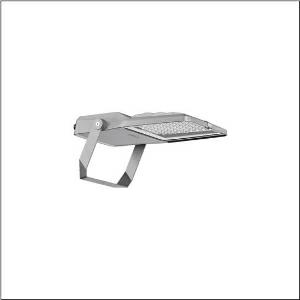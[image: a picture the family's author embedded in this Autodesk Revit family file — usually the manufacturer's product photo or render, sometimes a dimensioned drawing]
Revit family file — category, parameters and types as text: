
# Revit family: floodlight_fl_21_iq_mini___rs12_5xa7772c2b1a_7425
name_source: partatom
category: Lighting Fixtures
units: mm (PartAtom-declared; Revit-internal decimal feet)

## family parameters
Cut with Voids When Loaded = No
Host = Face
Light Source = No
Part Type = Normal
Room Calculation Point = No
Round Connector Dimension = Use Diameter
Shared = No

## types (1)
- --- (1 x LED, 12340 lm, 87.2 W, 3000K)
    Apparent Load = 87 VA
    CIE Flux Codes = 79 92 99 100 100
    Color Rendering = 70
    Color Temperature = 3000K
    Default Elevation = 1800 mm
    Description = Floodlight FL 21 iQ mini, floodlight, primary light control with lens, of PMMA, primary optical cover: protective disc, of toughened safety glass, transparent, light distribution: RS12, light emission: direct distribution, installation type: surface-mounted, LED, High Power LED, rated luminous flux: 12.340lm, luminous efficacy: 142lm/W, light colour: 730, colour temperature: 3000K, control gear: iQ Street-Remote/DALI, control: Street-Remote, Auto-Match, Temp-Guard, Night-Set, Smart-Wire, Desk-Remote (wireless, voltage-free reading and setting of iQ features in the workshop via application-optimized NFC function/RFID function), optimised constant luminous flux control (CLO 2.0), with terminal, 6-pole, mains connection: 220..240V, AC, 50/60Hz, start of lifetime: 87W, end of service life: 92W, reduction: 40W, luminaire housing, of diecast aluminium, powder-coated, Siteco® metallic grey (DB 702S), corrosivity category C5 mid according to DIN EN ISO 12944, suitable for swimming pools, chlorine-resistant, sealing non-destructively replaceable, mounting bracket, of steel, galvanised, powder-coated, Siteco® metallic grey (DB 702S), protection rating (complete): IP66, insulation class (complete): insulation class II (safety insulation), certification: CE, ENEC, VDE, protection symbol: D, impact resistance: IK08, permissible operating ambient temperature: -40..+40°C, permissible operating ambient temperature for outdoor applications: -40..+50°C, standard: DIN EN 12944, LABS conformity tested according to VDMA 24364:2018-05, packaging unit: 1 piece

Light Distribution: RS12
    Height = 70 mm
    Lamp = 1 x LED
    Lamp Light Flux = 12340 lm
    Lamp Power = 87.2 W
    Lamp count = 1
    Length = 485 mm
    Luminous efficacy = 142 lm/W
    Manufacturer = Siteco
    ModVariant = No
    Model = 5XA7772C2B1A
    Number of Poles = 1
    OnlyDefault = Yes
    Power Factor = 1
    Product Name = Floodlight FL 21 iQ mini | RS12
    Product group = floodlight | pylon annexe
    ProductGroupID = 6200
    Protection Class = Protection class II
    Protection Degree = IP 66
    RLX_Detail_Level = 1
    RLX_Emergency_Light_Flux = 0 lm
    RLX_Emergency_Type = 0
    RLX_Emergency_Type_DB = No
    RlxData = <blob elided: 91245 chars, md5=0f437b03>
    Socket = socket
    Standby Power = 0 W
    System Light Flux = 12340 lm
    System Power = 87 W
    Type Comments = factory setting: luminous flux: 100 % | dim-lin: 254 | 456 mA
    Type Image = l_1006845.jpg
    URL = http://relux.com
    VarID = @adj_167636
    Voltage = 0 V
    Weight = 0.00 kg
    Width = 337 mm

## geometry (parser evidence)
native form markers: Blend x4, Sweep x14
no freeform markers — native parametric forms only
